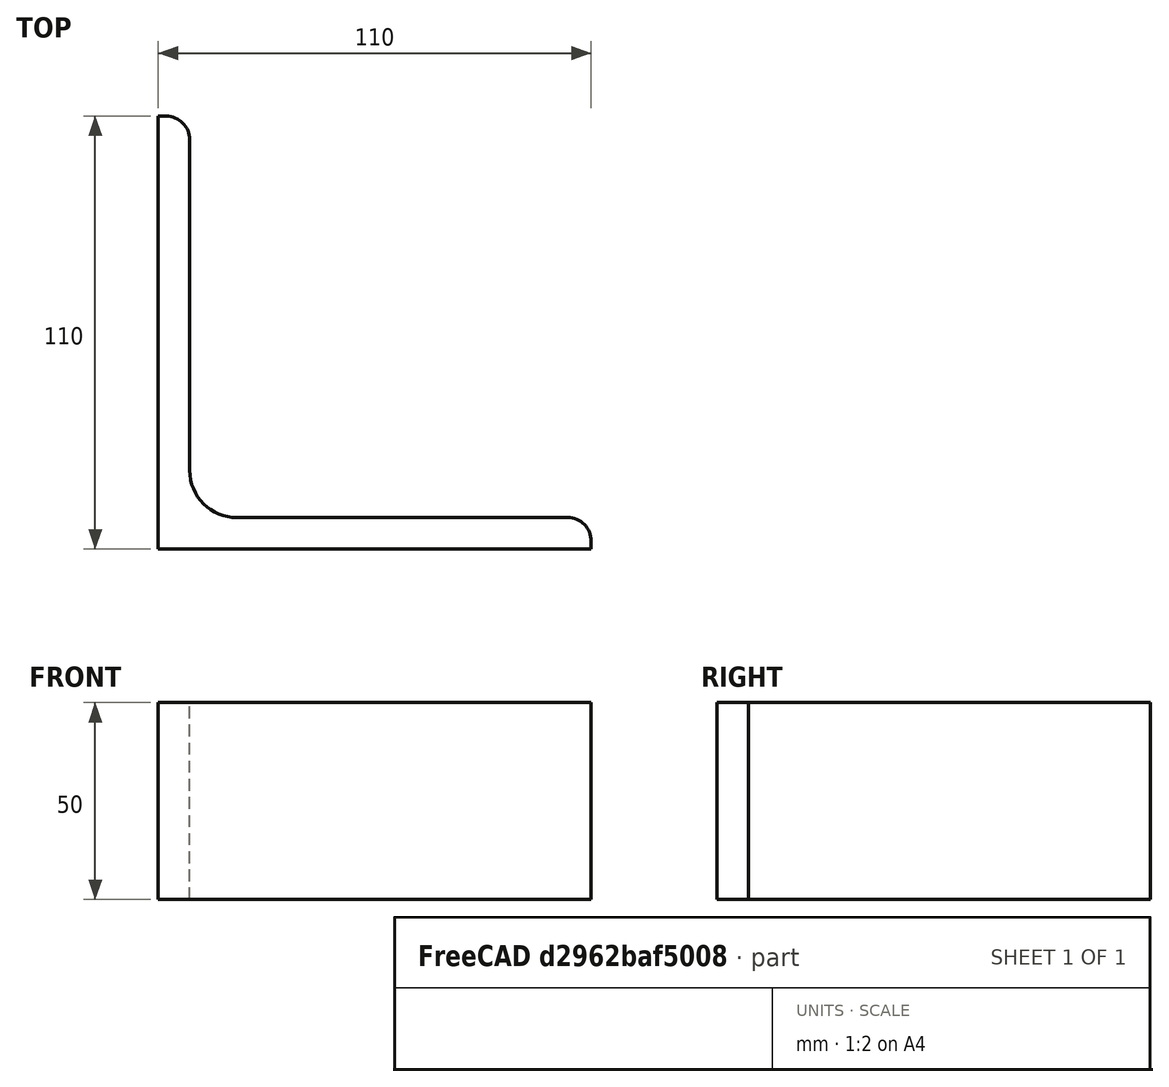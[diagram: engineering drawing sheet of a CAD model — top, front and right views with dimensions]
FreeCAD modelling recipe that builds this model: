
FCSTD DOCUMENT  (FreeCAD 0.15R4671 (Git))
Label: Angle Bar L110x110x8 EN10056 S235JR
License: All rights reserved
LicenseURL: http://en.wikipedia.org/wiki/All_rights_reserved
objects: Sketcher::SketchObject×1, Part::Extrusion×1
note: 2 computed .brp shape members not serialized (recipe doc carries the construction recipe); baked Part::Feature solids carry a one-line shape summary decoded from their .brp

FEATURE [Sketcher::SketchObject] Sketch
  sketch-geometry (9):
    g0: LineSegment StartX=0 StartY=0 StartZ=0 EndX=110 EndY=0 EndZ=0
    g1: LineSegment StartX=110 StartY=0 StartZ=0 EndX=110 EndY=2 EndZ=0
    g2: LineSegment StartX=104 StartY=8 StartZ=0 EndX=20 EndY=8 EndZ=0
    g3: LineSegment StartX=0 StartY=0 StartZ=0 EndX=0 EndY=110 EndZ=0
    g4: LineSegment StartX=0 StartY=110 StartZ=0 EndX=2 EndY=110 EndZ=0
    g5: LineSegment StartX=8 StartY=104 StartZ=0 EndX=8 EndY=20 EndZ=0
    g6: ArcOfCircle CenterX=20 CenterY=20 CenterZ=0 NormalX=0 NormalY=0 NormalZ=1 Radius=12 StartAngle=3.14159 EndAngle=4.71239
    g7: ArcOfCircle CenterX=2 CenterY=104 CenterZ=0 NormalX=0 NormalY=0 NormalZ=1 Radius=6 StartAngle=0 EndAngle=1.5708
    g8: ArcOfCircle CenterX=104 CenterY=2 CenterZ=0 NormalX=0 NormalY=0 NormalZ=1 Radius=6 StartAngle=0 EndAngle=1.5708
  constraints (23):
    c: Coincident(g0,g-1)
    c: Horizontal(g0)
    c: Coincident(g1,g0)
    c: Vertical(g1)
    c: Horizontal(g2)
    c: Coincident(g3,g-1)
    c: Vertical(g3)
    c: Coincident(g4,g3)
    c: Horizontal(g4)
    c: Vertical(g5)
    c: Tangent(g5,g6) = -1.5708
    c: Tangent(g2,g6) = 1.5708
    c: Tangent(g4,g7) = 1.5708
    c: Tangent(g5,g7) = 1.5708
    c: Tangent(g2,g8) = -1.5708
    c: Tangent(g1,g8) = -1.5708
    c: DistanceX(g0) = 110
    c: DistanceY(g3) = 110
    c: DistanceY(g0,g2) = 8
    c: DistanceX(g3,g5) = 8
    c: Radius(g6) = 12
    c: Radius(g8) = 6
    c: Radius(g7) = 6
FEATURE [Part::Extrusion] Extrude  label="Angle Bar L110x110x8 EN10056 S235JR"
  Base = -> Sketch
  Dir = (0,0,50)
  Solid = true
